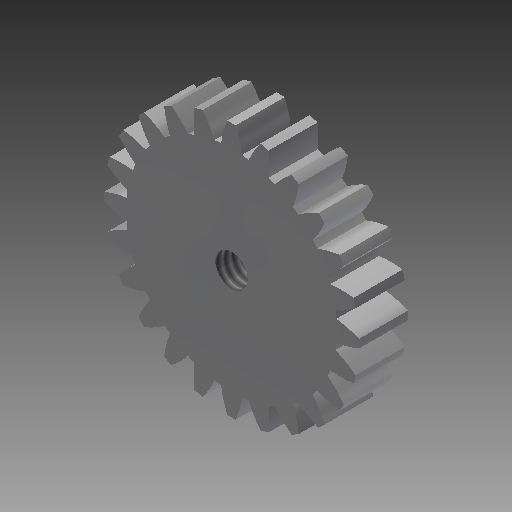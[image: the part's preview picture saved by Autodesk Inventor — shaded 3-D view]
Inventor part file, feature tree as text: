
AUTODESK INVENTOR PART (.ipt)
format: ipt  version: 2017 (Build 210142000, 142)  size: 242,688 bytes
history: native  units: mm (DEFAULTED — no unit token found)
features: plane x3, other x3, sketch x3, extrude x1, hole x1
ambient origin geometry x8: Origin, YZ Plane, XZ Plane, XY Plane, X Axis, Y Axis, Z Axis, Center Point
bodies: Solid1 (feature_tree)
feature tree (11):
  extrude  "Extrusion1"  Depth=5.0mm TaperAngle=0.0deg
  plane  "Work Plane2"
  plane  "Work Plane8"
  plane  "Work Plane9"
  other  "Spur Gear"
  hole  "Hole1"  [1 undecoded]
  sketch  "Sketch1"  dims[d0=26.0mm d1=5.0mm d2=0.0mm]
  sketch  "Sketch2"  dims[d3=24.0mm d4=10.0mm d5=0.0mm]
  other  "Srf1"
  sketch  "Sketch3"  dims[d16=18.0mm d17=0.0mm d34=1.308997mm d39=0.0mm d41=0.0mm d43=18.0mm d46=18.0mm d47=0.0mm d48=0.0mm d49=3.302mm d50=8.331mm d51=4.0mm d52=2.0mm d53=90.0deg d54=12.3mm d55=20.594885mm]
  other  "Pitch Diameter"
note: 1 required parameter value undecoded (feature->parameter linkage not recoverable at this tier; creation-order binding heuristic only, values carry confidence <= 0.55)
